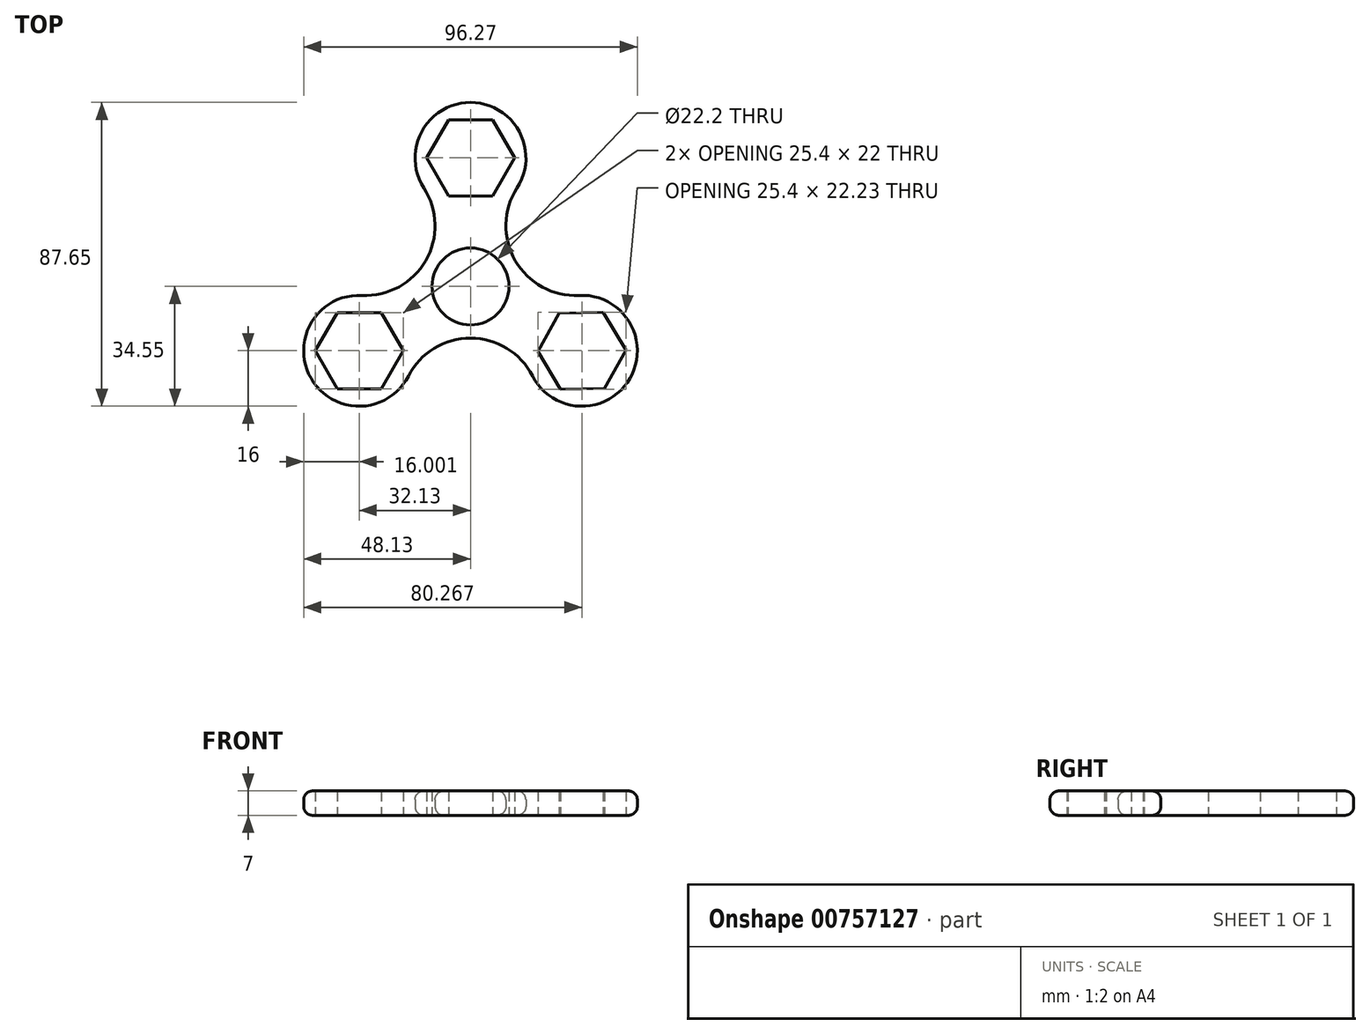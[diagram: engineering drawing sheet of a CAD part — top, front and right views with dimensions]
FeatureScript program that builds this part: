
annotation { "Feature Type Name" : "Feature", "Feature Type Description" : "" }
export const myFeature = defineFeature(function(context is Context, id is Id, definition is map)
    precondition{}
    {
        {
            var Q0;
            Q0=qCreatedBy(makeId("Top.planeOp"),FACE);
            var sketch = newSketch(context, id + "F0", { "sketchPlane" : qUnion([Q0])});
            skCircle(sketch, "E0", {"center": v(0, 0) * mm, "radius": 11.1 * mm});
            skLineSegment(sketch, "E1", {"start": v(0, 0) * mm, "end": v(0, 11.1) * mm});
            skCircle(sketch, "E2.cCircle", {"center": v(0, 37.1) * mm, "radius": 11 * mm, "construction": true});
            skLineSegment(sketch, "E2.0", {"start": v(12.7, 37.1) * mm, "end": v(6.35, 26.1) * mm});
            skLineSegment(sketch, "E2.1", {"start": v(6.35, 26.1) * mm, "end": v(-6.35, 26.1) * mm});
            skLineSegment(sketch, "E2.2", {"start": v(-6.35, 26.1) * mm, "end": v(-12.7, 37.1) * mm});
            skLineSegment(sketch, "E2.3", {"start": v(-12.7, 37.1) * mm, "end": v(-6.35, 48.1) * mm});
            skLineSegment(sketch, "E2.4", {"start": v(-6.35, 48.1) * mm, "end": v(6.35, 48.1) * mm});
            skLineSegment(sketch, "E2.5", {"start": v(6.35, 48.1) * mm, "end": v(12.7, 37.1) * mm});
            skPoint(sketch, "E2.0.midPoint", {"position": v(9.53, 31.6) * mm});
            skCircle(sketch, "E3.cCircle", {"center": v(-32.13, -18.55) * mm, "radius": 11 * mm, "construction": true});
            skLineSegment(sketch, "E3.0", {"start": v(-44.83, -18.55) * mm, "end": v(-38.48, -7.55) * mm});
            skLineSegment(sketch, "E3.1", {"start": v(-38.48, -7.55) * mm, "end": v(-25.78, -7.55) * mm});
            skLineSegment(sketch, "E3.2", {"start": v(-25.78, -7.55) * mm, "end": v(-19.43, -18.55) * mm});
            skLineSegment(sketch, "E3.3", {"start": v(-19.43, -18.55) * mm, "end": v(-25.78, -29.55) * mm});
            skLineSegment(sketch, "E3.4", {"start": v(-25.78, -29.55) * mm, "end": v(-38.48, -29.55) * mm});
            skLineSegment(sketch, "E3.5", {"start": v(-38.48, -29.55) * mm, "end": v(-44.83, -18.55) * mm});
            skPoint(sketch, "E3.0.midPoint", {"position": v(-41.66, -13.05) * mm});
            skCircle(sketch, "E4.cCircle", {"center": v(32.14, -18.55) * mm, "radius": 11 * mm, "construction": true});
            skLineSegment(sketch, "E4.0", {"start": v(38.28, -7.43) * mm, "end": v(44.84, -18.31) * mm});
            skLineSegment(sketch, "E4.1", {"start": v(44.84, -18.31) * mm, "end": v(38.7, -29.43) * mm});
            skLineSegment(sketch, "E4.2", {"start": v(38.7, -29.43) * mm, "end": v(26, -29.67) * mm});
            skLineSegment(sketch, "E4.3", {"start": v(26, -29.67) * mm, "end": v(19.44, -18.79) * mm});
            skLineSegment(sketch, "E4.4", {"start": v(19.44, -18.79) * mm, "end": v(25.58, -7.67) * mm});
            skLineSegment(sketch, "E4.5", {"start": v(25.58, -7.67) * mm, "end": v(38.28, -7.43) * mm});
            skPoint(sketch, "E4.0.midPoint", {"position": v(41.56, -12.87) * mm});
            skLineSegment(sketch, "E5", {"start": v(0, 0) * mm, "end": v(0, -11.1) * mm});
            skArc(sketch, "E6.trimOffspring", {"start": v(25.52, -7.67) * mm, "mid": v(27.14, -7.93) * mm, "end": v(28.77, -8.08) * mm});
            skPoint(sketch, "E7.center.orphan", {"position": v(-30.31, 17.5) * mm});
            skArc(sketch, "E8.trimOffspring", {"start": v(34.43, -7.8) * mm, "mid": v(36.22, -7.43) * mm, "end": v(37.99, -6.95) * mm});
            skPoint(sketch, "E9.center.orphan", {"position": v(0, -35) * mm});
            skLineSegment(sketch, "E10.trimOffspring", {"start": v(41.73, -23.94) * mm, "end": v(41.87, -24.02) * mm});
            skArc(sketch, "E11", {"start": v(13.44, 28.41) * mm, "mid": v(0, 53.1) * mm, "end": v(-13.44, 28.41) * mm});
            skArc(sketch, "E12", {"start": v(17.9, -25.84) * mm, "mid": v(46, -26.55) * mm, "end": v(31.33, -2.57) * mm});
            skArc(sketch, "E13", {"start": v(-31.32, -2.57) * mm, "mid": v(-45.99, -26.55) * mm, "end": v(-17.89, -25.84) * mm});
            skArc(sketch, "E14", {"start": v(-31.32, -2.57) * mm, "mid": v(-12.9, 7.45) * mm, "end": v(-13.44, 28.41) * mm});
            skArc(sketch, "E15", {"start": v(13.44, 28.41) * mm, "mid": v(12.9, 7.45) * mm, "end": v(31.33, -2.57) * mm});
            skArc(sketch, "E16", {"start": v(17.9, -25.84) * mm, "mid": v(0, -14.9) * mm, "end": v(-17.89, -25.84) * mm});
            skLineSegment(sketch, "E17", {"start": v(0, 0) * mm, "end": v(65.93, 38.07) * mm});
            skSolve(sketch);
        }
        {
            var Q0;
            {var subQ10=sQuery(id+"F0.wireOp",EDGE,"E2.0");Q0=makeQuery(id+"F0.imprint","IMPRINT",FACE,{"disambiguationData":[TD([[makeQuery(id+"F0.imprint","IMPRINT",EDGE,{"derivedFrom":subQ10}),1.0]])]});}
            extrude(context, id + "F1", {"entities" : qUnion([Q0]), "depth" : 7 * mm, "offsetDistance" : 25 * mm});
        }
        {
            var Q0;
            Q0=makeQuery(id+"F1.opExtrude","CAP_EDGE",EDGE,{"disambiguationData":[OSD([sQuery(id+"F0.wireOp",EDGE,"E12")])],"isStart":false});
            fillet(context, id + "F2", {"entities" : qUnion([Q0]), "radius" : 2.5 * mm, "tangentPropagation" : true, "allowEdgeOverflow" : false});
        }
        {
            var Q0;
            Q0=makeQuery(id+"F1.opExtrude","CAP_EDGE",EDGE,{"disambiguationData":[OSD([sQuery(id+"F0.wireOp",EDGE,"E13")])],"isStart":true});
            fillet(context, id + "F3", {"entities" : qUnion([Q0]), "radius" : 2.5 * mm, "tangentPropagation" : true, "allowEdgeOverflow" : false});
        }
    });
